# Revit family: P2I_2903-2943-2606_OS275
name_source: partatom
category: Porte
units: mm (PartAtom-declared; Revit-internal decimal feet)

## family parameters
Condiviso = No
Host = Muro
Numero OmniClass = 23.30.10.00
Punto di calcolo locali = Sì
Sempre verticale = Sì
Taglio con vuoti quando caricato = No
Titolo OmniClass = Doors

## types (4) — shared parameters
Chiusura muro = Per host
Costruzione analitica = <Nessuno>
Descrizione = Porta ad un'anta, apertura interna
Funzione = Interno
H_Max = 2900 mm
H_Min = 1600 mm  [stored 5.24934 ft]
H_maniglia = 1000 mm  [stored 3.28084 ft]
L_Max = 2000 mm  [stored 6.56168 ft]
L_Min = 600 mm
Larghezza telaio = 75 mm
Modello = OS2 75
Produttore = Secco Sistemi Spa
Proiezione telaio est. = 25 mm  [stored 0.082021 ft]
Proiezione telaio int. = 25 mm  [stored 0.082021 ft]
URL = https://www.seccosistemi.com
n2_cerniere = 2
n3_cerniere = 3
n4_cerniere = 4
numero_cerniere = 3

## per-type parameters (varying)
| type | Altezza | H | H1 | H_vetro | L | L1 | L_vetro | Larghezza | Larghezza_1A | Larghezza_2A | MATERIALE | WARNING |
| Acciaio Zincato | 2500 mm  [stored 8.2021 ft] | 2500 mm  [stored 8.2021 ft] | 2500 mm  [stored 8.2021 ft] | 2424 mm  [stored 7.95276 ft] | 2000 mm  [stored 6.56168 ft] | 2000 mm  [stored 6.56168 ft] | 940 mm  [stored 3.08399 ft] | 2000 mm  [stored 6.56168 ft] | 1016 mm  [stored 3.33333 ft] | 1016 mm  [stored 3.33333 ft] | Acciaio | No |
| Acciaio Inox | 2000 mm  [stored 6.56168 ft] | 2000 mm  [stored 6.56168 ft] | 2000 mm  [stored 6.56168 ft] | 1924 mm  [stored 6.31234 ft] | 900 mm  [stored 2.95276 ft] | 900 mm  [stored 2.95276 ft] | 390 mm | 900 mm  [stored 2.95276 ft] | 466 mm | 466 mm | Acciaio inox, spazzolato | No |
| Acciaio Corten | 1500 mm | 1600 mm  [stored 5.24934 ft] | 1600 mm  [stored 5.24934 ft] | 1524 mm  [stored 5 ft] | 1500 mm | 1500 mm | 690 mm | 1500 mm | 766 mm  [stored 2.51312 ft] | 766 mm  [stored 2.51312 ft] | Acciaio corten | Sì |
| Ottone | 2000 mm  [stored 6.56168 ft] | 2000 mm  [stored 6.56168 ft] | 2000 mm  [stored 6.56168 ft] | 1924 mm  [stored 6.31234 ft] | 900 mm  [stored 2.95276 ft] | 900 mm  [stored 2.95276 ft] | 390 mm | 900 mm  [stored 2.95276 ft] | 466 mm | 466 mm | Ottone | No |

note: [stored X ft] marks values corroborated as IEEE doubles in the binary element streams (Revit-internal decimal feet)
